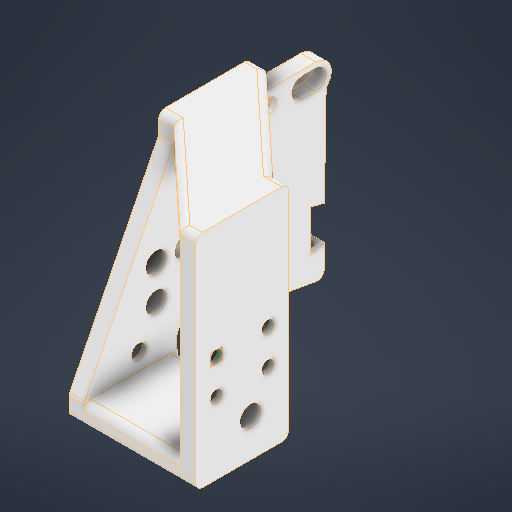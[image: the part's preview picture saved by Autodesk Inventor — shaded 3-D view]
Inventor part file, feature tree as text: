
AUTODESK INVENTOR PART (.ipt)
format: ipt  version: 2025 (Build 290162000, 162)  size: 502,272 bytes
history: native  units: mm
features: extrude x10, sketch x10, reference x5, other x5, projected_geometry x2, plane x1, fillet x1
ambient origin geometry x8: Origin, YZ Plane, XZ Plane, XY Plane, X Axis, Y Axis, Z Axis, Center Point
bodies: Solid1 (feature_tree)
feature tree (34):
  plane  "Work Plane1"
  extrude  "Extrusion1"  Depth=6.0mm
  extrude  "Extrusion2"  Depth=6.0mm
  extrude  "Extrusion3"  Depth=3.5mm
  extrude  "Extrusion4"  Depth=3.5mm
  extrude  "Extrusion5"  Depth=6.0mm
  extrude  "Extrusion6"  Depth=6.0mm
  extrude  "Extrusion7"  Depth=6.0mm TaperAngle=0.0deg
  extrude  "Extrusion8"  Depth=10.0mm TaperAngle=0.0deg
  extrude  "Extrusion9"  Depth=6.0mm TaperAngle=0.0deg
  extrude  "Extrusion10"  Depth=10.0mm TaperAngle=0.0deg
  fillet  "Fillet1"  Radius=27.0mm
  sketch  "Sketch1"  dims[d0=6.0mm d1=6.0mm]
  reference  "Reference1"
  reference  "Reference2"
  reference  "Reference3"
  reference  "Reference4"
  sketch  "Sketch2"  dims[d2=6.0mm d3=6.0mm]
  sketch  "Sketch3"  dims[d4=3.5mm d5=3.5mm]
  projected_geometry  "Projected Loop1"
  sketch  "Sketch4"  dims[d6=3.5mm d7=3.5mm]
  sketch  "Sketch5"  dims[d8=4.5mm d9=0.0mm d10=6.0mm]
  sketch  "Sketch6"  dims[d11=6.0mm d12=6.0mm]
  projected_geometry  "Projected Loop2"
  sketch  "Sketch7"  dims[d13=6.0mm d14=3.0mm d15=0.0mm]
  sketch  "Sketch8"  dims[d16=3.0mm d17=0.0mm d18=10.0mm d19=0.0mm]
  sketch  "Sketch9"  dims[d20=27.0mm d21=6.0mm d22=0.0mm]
  reference  "Reference5"
  sketch  "Sketch10"  dims[d23=4.999996mm d24=10.0mm d25=0.0mm d26=27.0mm d27=6.0mm d28=0.0mm d29=6.0mm d30=0.0mm d31=6.0mm d32=10.0mm d33=0.0mm d34=6.0mm d35=0.0mm d37=2.0mm]
  other  "Part 2"
  other  "hotend-new.iam"
  other  "bolts reference:1"
  other  "Radial_Fan_50x15 v8:1"
  other  "Finish1"
